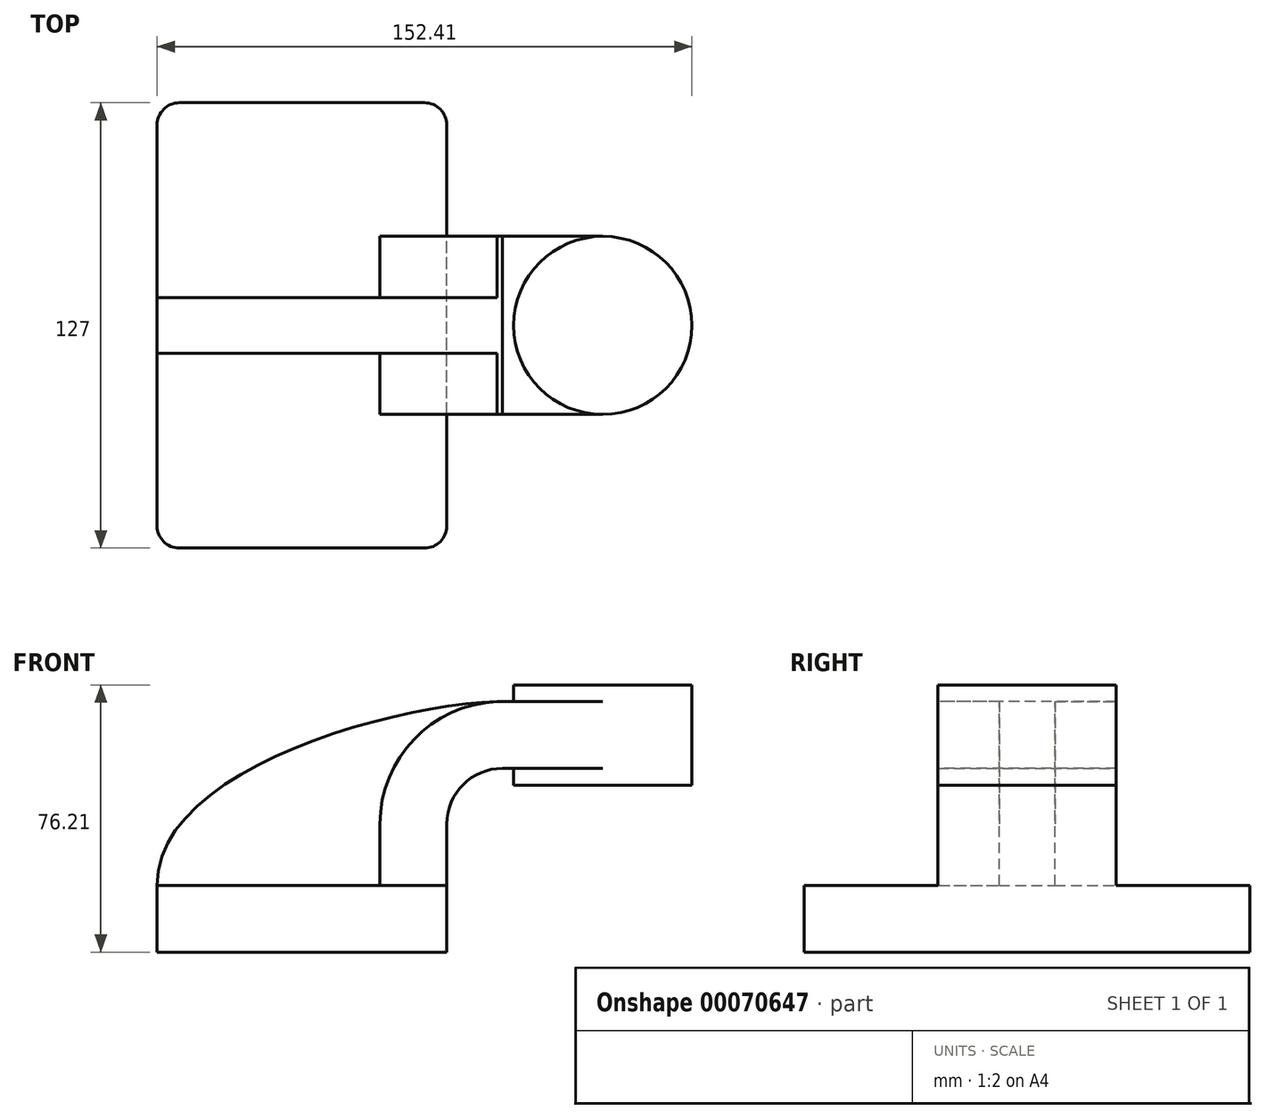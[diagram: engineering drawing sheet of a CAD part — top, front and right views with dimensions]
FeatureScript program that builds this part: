
annotation { "Feature Type Name" : "Feature", "Feature Type Description" : "" }
export const myFeature = defineFeature(function(context is Context, id is Id, definition is map)
    precondition{}
    {
        {
            var Q0;
            Q0=qCreatedBy(makeId("Front.planeOp"),FACE);
            var sketch = newSketch(context, id + "F0", { "sketchPlane" : qUnion([Q0])});
            skLineSegment(sketch, "E0.rect.bottom", {"start": v(-41.28, -9.53) * mm, "end": v(41.28, -9.53) * mm});
            skLineSegment(sketch, "E0.rect.top", {"start": v(-41.28, 9.52) * mm, "end": v(41.28, 9.52) * mm});
            skLineSegment(sketch, "E0.rect.left", {"start": v(-41.28, -9.53) * mm, "end": v(-41.28, 9.53) * mm});
            skLineSegment(sketch, "E0.rect.right", {"start": v(41.28, -9.53) * mm, "end": v(41.28, 9.52) * mm});
            skPoint(sketch, "E0.rect.middle", {"position": v(0, 0) * mm});
            skLineSegment(sketch, "E1.rect.bottom", {"start": v(60.32, 38.1) * mm, "end": v(111.12, 38.1) * mm});
            skLineSegment(sketch, "E1.rect.top", {"start": v(60.32, 66.68) * mm, "end": v(111.12, 66.68) * mm});
            skLineSegment(sketch, "E1.rect.left", {"start": v(60.32, 38.1) * mm, "end": v(60.32, 66.67) * mm});
            skLineSegment(sketch, "E1.rect.right", {"start": v(111.12, 38.1) * mm, "end": v(111.12, 66.67) * mm});
            skPoint(sketch, "E1.rect.middle", {"position": v(85.72, 52.39) * mm});
            skLineSegment(sketch, "E2", {"start": v(41.28, 9.52) * mm, "end": v(41.28, 27) * mm});
            skArc(sketch, "E3", {"start": v(41.28, 27) * mm, "mid": v(45.92, 38.23) * mm, "end": v(57.15, 42.88) * mm});
            skLineSegment(sketch, "E4", {"start": v(57.15, 42.88) * mm, "end": v(85.72, 42.88) * mm});
            skArc(sketch, "E5.0", {"start": v(22.23, 27) * mm, "mid": v(32.45, 51.7) * mm, "end": v(57.15, 61.93) * mm});
            skLineSegment(sketch, "E6.0", {"start": v(22.23, 9.52) * mm, "end": v(22.23, 27) * mm});
            skLineSegment(sketch, "E7.0", {"start": v(57.15, 61.93) * mm, "end": v(85.72, 61.93) * mm});
            skFitSpline(sketch, "E8", {"points": [v(-41.28, 9.53) * mm, v(57.15, 61.93) * mm], "startDerivative": vector(-1.46, 98.82) * mm, "endDerivative": vector(92.84, 1.17) * mm});
            skLineSegment(sketch, "E9", {"start": v(85.72, 61.93) * mm, "end": v(85.72, 66.67) * mm});
            skLineSegment(sketch, "E10", {"start": v(85.72, 61.93) * mm, "end": v(85.72, 42.88) * mm});
            skLineSegment(sketch, "E11", {"start": v(85.72, 42.88) * mm, "end": v(85.72, 38.1) * mm});
            skSolve(sketch);
        }
        {
            var Q0;
            Q0=makeQuery(id+"F0.imprint","IMPRINT",FACE,{"disambiguationData":[TD([[makeQuery(id+"F0.imprint","IMPRINT",EDGE,{"derivedFrom":sQuery(id+"F0.wireOp",EDGE,"E0.rect.bottom")}),1.0]])]});
            extrude(context, id + "F1", {"entities" : qUnion([Q0]), "endBound" : BoundingType.SYMMETRIC, "depth" : 127 * mm});
        }
        {
            var Q0;
            {var subQ1=sQuery(id+"F0.wireOp",EDGE,"E2");Q0=makeQuery(id+"F0.imprint","IMPRINT",FACE,{"disambiguationData":[TD([[makeQuery(id+"F0.imprint","IMPRINT",EDGE,{"derivedFrom":subQ1}),1.0]])]});}
            var Q1;
            {var subQ5=sQuery(id+"F0.wireOp",EDGE,"E10");Q1=makeQuery(id+"F0.imprint","IMPRINT",FACE,{"disambiguationData":[TD([[makeQuery(id+"F0.imprint","IMPRINT",EDGE,{"derivedFrom":subQ5}),-1.0]])]});}
            extrude(context, id + "F2", {"entities" : qUnion([Q0, Q1]), "operationType" : NewBodyOperationType.ADD, "endBound" : BoundingType.SYMMETRIC, "depth" : 50.8 * mm});
        }
        {
            var Q0;
            {var subQ3=sQuery(id+"F0.wireOp",EDGE,"E6.0");Q0=makeQuery(id+"F0.imprint","IMPRINT",FACE,{"disambiguationData":[TD([[makeQuery(id+"F0.imprint","IMPRINT",EDGE,{"derivedFrom":subQ3}),1.0]])]});}
            extrude(context, id + "F3", {"entities" : qUnion([Q0]), "operationType" : NewBodyOperationType.ADD, "endBound" : BoundingType.SYMMETRIC, "depth" : 15.88 * mm});
        }
        {
            var Q0;
            {var subQ0=sQuery(id+"F0.wireOp",EDGE,"E1.rect.right");Q0=makeQuery(id+"F0.imprint","IMPRINT",FACE,{"disambiguationData":[TD([[makeQuery(id+"F0.imprint","IMPRINT",EDGE,{"derivedFrom":subQ0}),1.0]])]});}
            var Q1;
            Q1=sQuery(id+"F0.wireOp",EDGE,"E10");
            revolve(context, id + "F4", {"operationType" : NewBodyOperationType.ADD, "entities" : qUnion([Q0]), "axis" : qUnion([Q1]), "revolveType" : RevolveType.FULL});
        }
        {
            var Q0;
            Q0=makeQuery(id+"F1.opExtrude","CAP_EDGE",EDGE,{"disambiguationData":[OSD([sQuery(id+"F0.wireOp",EDGE,"E0.rect.right")])],"isStart":false});
            var Q1;
            Q1=makeQuery(id+"F1.opExtrude","CAP_EDGE",EDGE,{"disambiguationData":[OSD([sQuery(id+"F0.wireOp",EDGE,"E0.rect.left")])],"isStart":false});
            var Q2;
            Q2=makeQuery(id+"F1.opExtrude","CAP_EDGE",EDGE,{"disambiguationData":[OSD([sQuery(id+"F0.wireOp",EDGE,"E0.rect.right")])],"isStart":true});
            var Q3;
            Q3=makeQuery(id+"F1.opExtrude","CAP_EDGE",EDGE,{"disambiguationData":[OSD([sQuery(id+"F0.wireOp",EDGE,"E0.rect.left")])],"isStart":true});
            fillet(context, id + "F5", {"entities" : qUnion([Q0, Q1, Q2, Q3]), "radius" : 6.35 * mm, "tangentPropagation" : true, "allowEdgeOverflow" : false});
        }
    });
